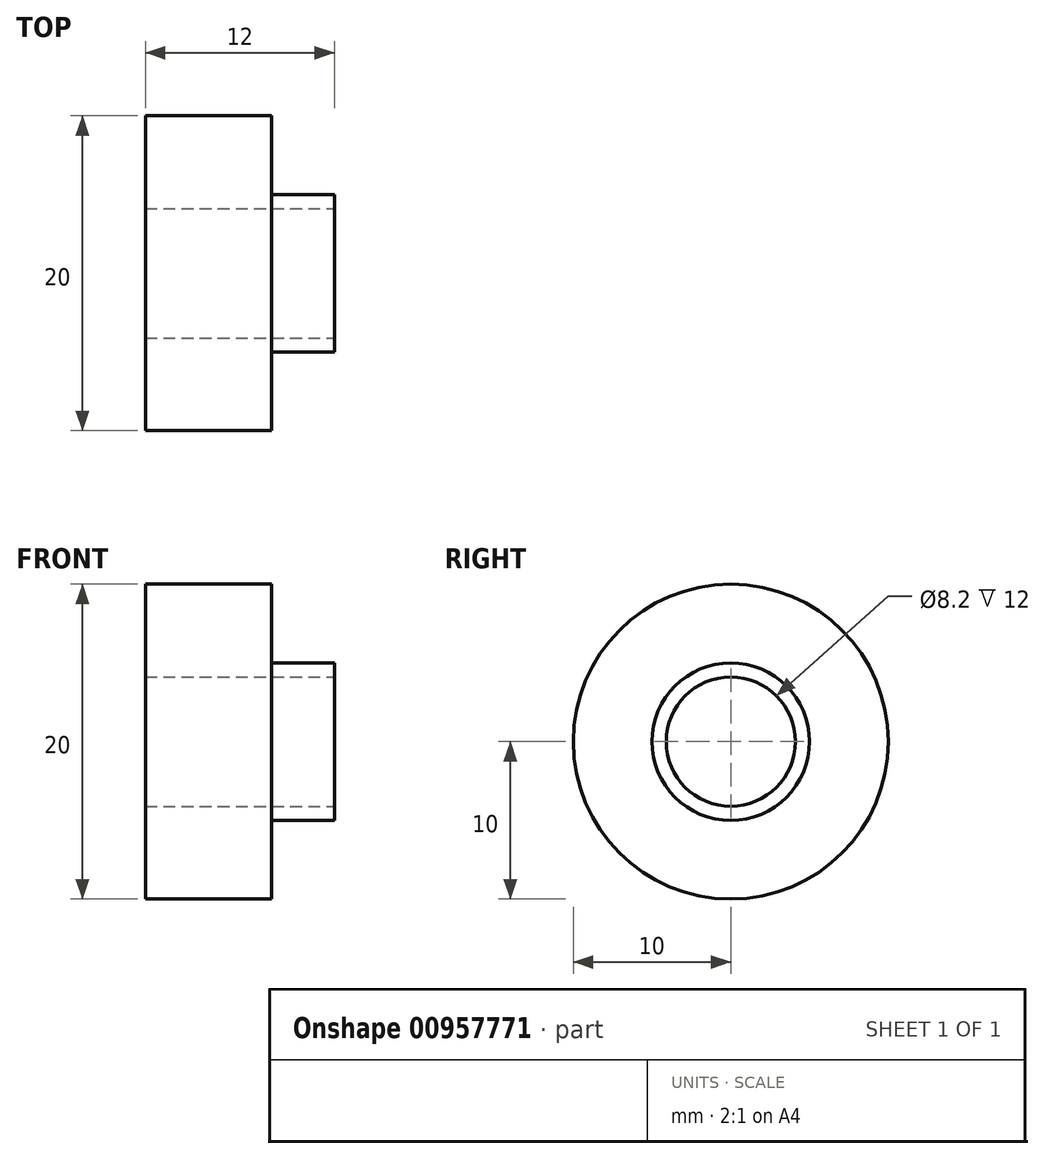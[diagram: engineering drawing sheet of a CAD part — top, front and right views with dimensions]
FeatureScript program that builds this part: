
annotation { "Feature Type Name" : "Feature", "Feature Type Description" : "" }
export const myFeature = defineFeature(function(context is Context, id is Id, definition is map)
    precondition{}
    {
        {
            var Q0;
            Q0=qCreatedBy(makeId("Top.planeOp"),FACE);
            var sketch = newSketch(context, id + "F0", { "sketchPlane" : qUnion([Q0])});
            skLineSegment(sketch, "E0", {"start": v(0, 4.1) * mm, "end": v(12, 4.1) * mm});
            skLineSegment(sketch, "E1", {"start": v(12, 4.1) * mm, "end": v(12, 5) * mm});
            skLineSegment(sketch, "E2", {"start": v(12, 5) * mm, "end": v(8, 5) * mm});
            skLineSegment(sketch, "E3", {"start": v(8, 5) * mm, "end": v(8, 10) * mm});
            skLineSegment(sketch, "E4", {"start": v(8, 10) * mm, "end": v(0, 10) * mm});
            skLineSegment(sketch, "E5", {"start": v(0, 10) * mm, "end": v(0, 4.1) * mm});
            skLineSegment(sketch, "E6", {"start": v(-1.48, 0) * mm, "end": v(9.26, 0) * mm, "construction": true});
            skSolve(sketch);
        }
        {
            var Q0;
            Q0=sQuery(id+"F0.wireOp",EDGE,"E4");
            var Q1;
            Q1=sQuery(id+"F0.wireOp",EDGE,"E2");
            var Q2;
            Q2=sQuery(id+"F0.wireOp",EDGE,"E3");
            var Q3;
            Q3=sQuery(id+"F0.wireOp",EDGE,"E5");
            var Q4;
            Q4=sQuery(id+"F0.wireOp",EDGE,"E0");
            var Q5;
            Q5=sQuery(id+"F0.wireOp",EDGE,"E1");
            var Q6;
            Q6=sQuery(id+"F0.wireOp",EDGE,"E6");
            revolve(context, id + "F1", {"bodyType" : ToolBodyType.SURFACE, "surfaceOperationType" : NewSurfaceOperationType.NEW, "surfaceEntities" : qUnion([Q0, Q1, Q2, Q3, Q4, Q5]), "axis" : qUnion([Q6]), "revolveType" : RevolveType.FULL});
        }
    });
